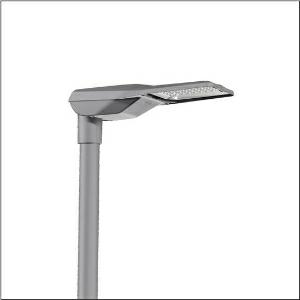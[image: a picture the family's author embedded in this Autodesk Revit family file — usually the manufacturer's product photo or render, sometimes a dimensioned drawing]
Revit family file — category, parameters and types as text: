
# Revit family: streetlight_sl_21_iq_mini___p0_8a_5xe2u31d08gb_8910
name_source: partatom
category: Lighting Fixtures
units: mm (PartAtom-declared; Revit-internal decimal feet)

## family parameters
Cut with Voids When Loaded = No
Host = Face
Light Source = No
Part Type = Normal
Room Calculation Point = No
Round Connector Dimension = Use Diameter
Shared = No

## types (1)
- --- (1 x LED, 5730 lm, 37.1 W, 3000K)
    Apparent Load = 37 VA
    CIE Flux Codes = 33 69 96 100 100
    Color Rendering = 70
    Color Temperature = 3000K
    Default Elevation = 1800 mm
    Description = Streetlight SL 21 iQ mini, mast luminaire, primary light control with lens, of PMMA, primary optical cover: cover, of toughened safety glass, transparent, light distribution: P0.8a, light emission: direct distribution, primary light characteristic: asymmetric, installation type: post-top, side-entry, LED, High Power LED, rated luminous flux: 5.730lm, luminous efficacy: 154lm/W, light colour: 730, colour temperature: 3000K, control gear: iQ-Comfort, control: pre-setting: linear dimming characteristic, Auto-Match, Temp-Guard, Lumen-Switch, Night-Set, Smart-Wire, Light-Fading, Desk-Remote (wireless, voltage-free reading and setting of iQ features in the workshop via application-optimized NFC function/RFID function), optimised constant luminous flux control (CLO 2.0), mains connection: 220..240V, AC, 50/60Hz, start of lifetime: 37W, end of service life: 39W, reduction: 18W, luminaire housing, of diecast aluminium, powder-coated, Siteco® metallic grey (DB 702S), corrosivity category C5 mid according to DIN EN ISO 12944, please order mast flange separately, inclination adjustable: 0°, 5°, 10°, 15°, sealing non-destructively replaceable, multi-level sealing system, length: 628mm, width: 235mm, height: 110mm, mast flange for spigot size: 42mm (side-entry): 5XC10008XM4, 60/48mm (side-entry/post-top): 5XC10108XM2, 76/60mm (side-entry/post-top): 5XC10108XM1, mounting height: 4..8m, protection rating (complete): IP66, insulation class (complete): insulation class II (safety insulation), certification: CE, ENEC, ENEC+, VDE, impact resistance: IK09, permissible operating ambient temperature for outdoor applications: -40..+50°C, standard-compliant lighting for roads and squares, packaging unit: 1 piece

Light Distribution: P0.8a
    Height = 110 mm
    Lamp = 1 x LED
    Lamp Light Flux = 5730 lm
    Lamp Power = 37.1 W
    Lamp count = 1
    Length = 625 mm
    Luminous efficacy = 154 lm/W
    Manufacturer = Siteco
    ModVariant = No
    Model = 5XE2U31D08GB
    Number of Poles = 1
    OnlyDefault = Yes
    Power Factor = 1
    Product Name = Streetlight SL 21 iQ mini | P0.8a
    Product group = mast luminaire | pylon top
    ProductGroupID = 6100
    Protection Class = Protection class II
    Protection Degree = IP 66
    RLX_Detail_Level = 1
    RLX_Emergency_Light_Flux = 0 lm
    RLX_Emergency_Type = 0
    RLX_Emergency_Type_DB = No
    RlxData = <blob elided: 91997 chars, md5=f42dbf84>
    Socket = socket
    Standby Power = 0 W
    System Light Flux = 5730 lm
    System Power = 37 W
    Type Comments = factory setting: luminous flux: 100 % | dim-lin: 254 | 385 mA
    Type Image = l_1003519.jpg
    URL = http://relux.com
    VarID = @adj_069706
    Voltage = 0 V
    Weight = 0.00 kg
    Width = 234 mm

## geometry (parser evidence)
native form markers: Blend x4, Sweep x13
no freeform markers — native parametric forms only
